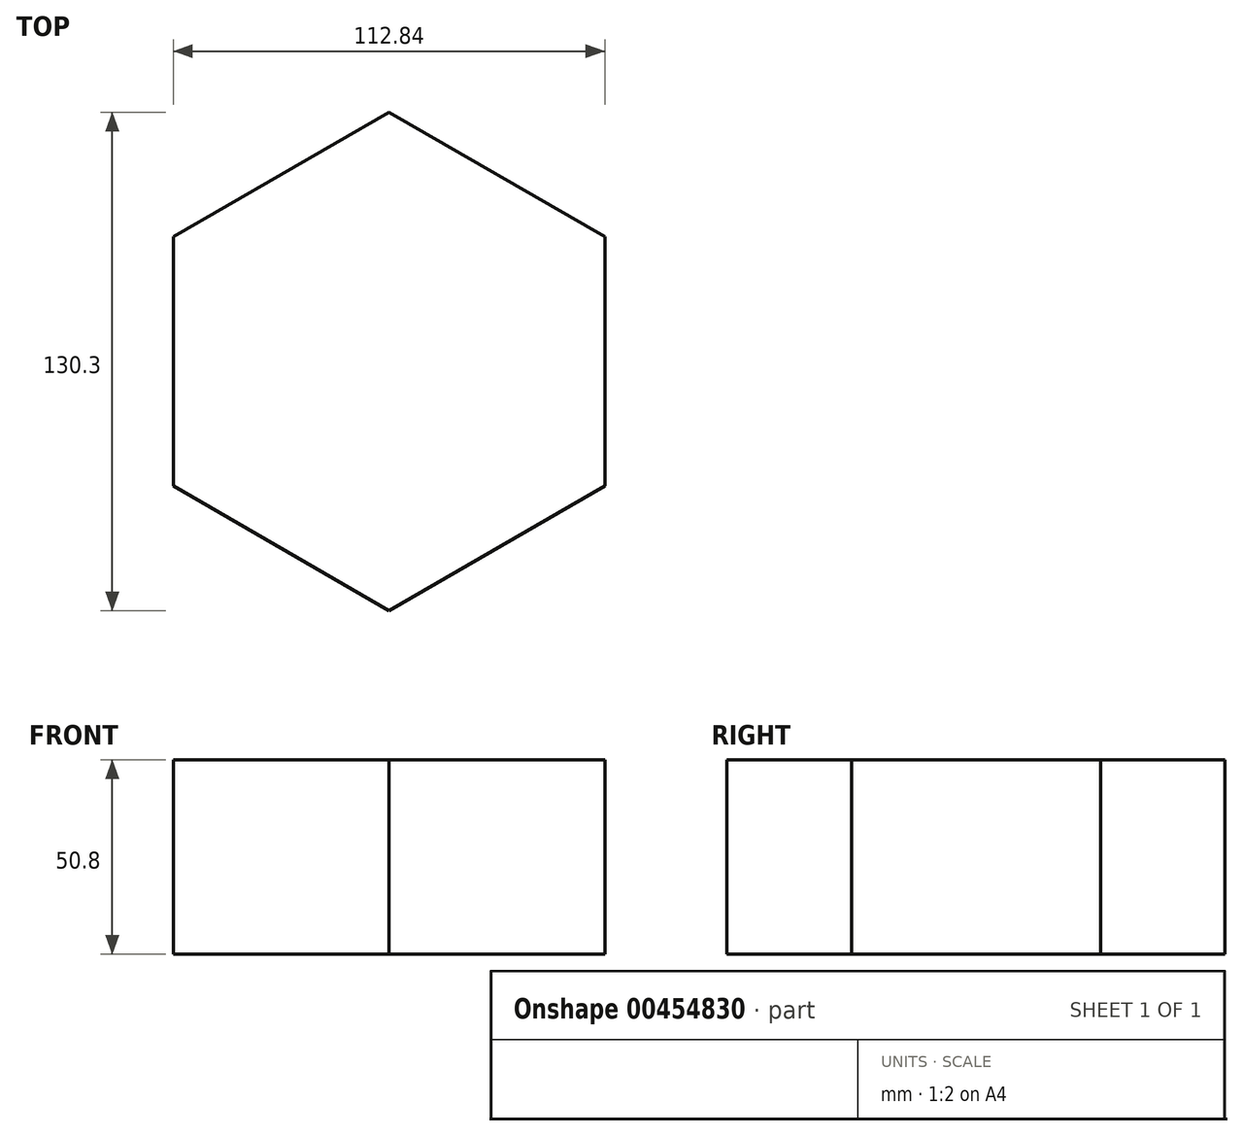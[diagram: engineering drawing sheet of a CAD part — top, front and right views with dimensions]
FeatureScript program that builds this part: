
annotation { "Feature Type Name" : "Feature", "Feature Type Description" : "" }
export const myFeature = defineFeature(function(context is Context, id is Id, definition is map)
    precondition{}
    {
        {
            var Q0;
            Q0=qCreatedBy(makeId("Top.planeOp"),FACE);
            var sketch = newSketch(context, id + "F0", { "sketchPlane" : qUnion([Q0])});
            skCircle(sketch, "E0.cCircle", {"center": v(0, 0) * mm, "radius": 56.42 * mm, "construction": true});
            skLineSegment(sketch, "E0.0", {"start": v(56.42, 32.58) * mm, "end": v(56.42, -32.58) * mm});
            skLineSegment(sketch, "E0.1", {"start": v(56.42, -32.58) * mm, "end": v(0, -65.15) * mm});
            skLineSegment(sketch, "E0.2", {"start": v(0, -65.15) * mm, "end": v(-56.42, -32.58) * mm});
            skLineSegment(sketch, "E0.3", {"start": v(-56.42, -32.58) * mm, "end": v(-56.42, 32.58) * mm});
            skLineSegment(sketch, "E0.4", {"start": v(-56.42, 32.58) * mm, "end": v(0, 65.15) * mm});
            skLineSegment(sketch, "E0.5", {"start": v(0, 65.15) * mm, "end": v(56.42, 32.58) * mm});
            skPoint(sketch, "E0.0.midPoint", {"position": v(56.42, 0) * mm});
            skSolve(sketch);
        }
        {
            var Q0;
            Q0 = qSketchRegion(id + "F0", true);
            extrude(context, id + "F1", {"entities" : qUnion([Q0]), "depth" : 50.8 * mm});
        }
    });
